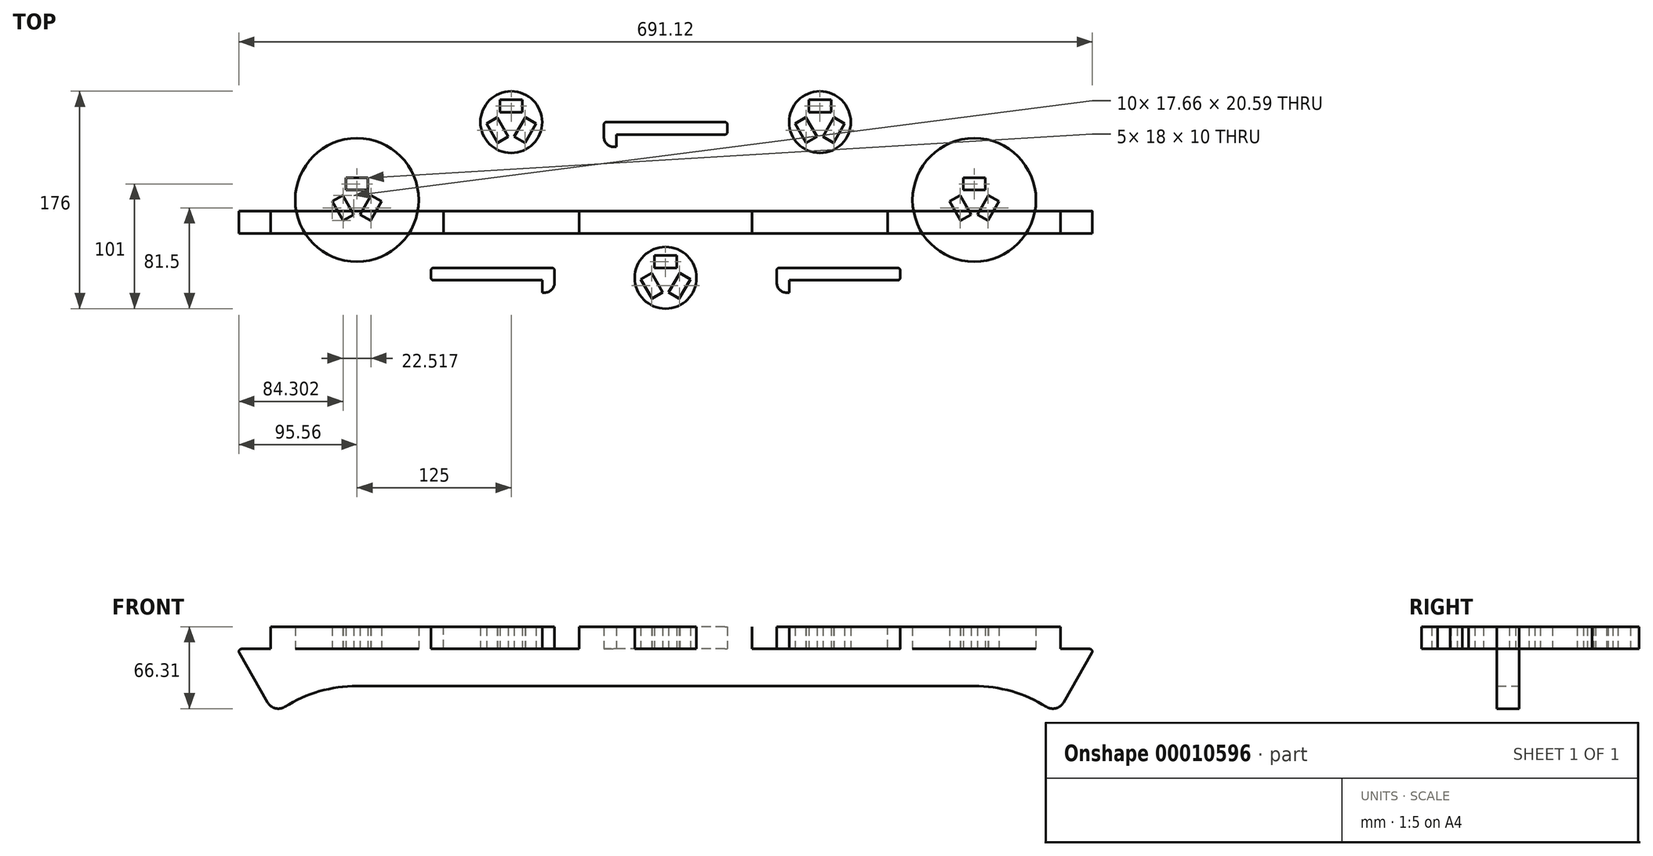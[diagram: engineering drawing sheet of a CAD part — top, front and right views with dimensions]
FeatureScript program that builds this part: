
annotation { "Feature Type Name" : "Feature", "Feature Type Description" : "" }
export const myFeature = defineFeature(function(context is Context, id is Id, definition is map)
    precondition{}
    {
        {
            var Q0;
            Q0=qCreatedBy(makeId("Top.planeOp"),FACE);
            var sketch = newSketch(context, id + "F0", { "sketchPlane" : qUnion([Q0])});
            skLineSegment(sketch, "E0.bottom", {"start": v(-250, 100) * mm, "end": v(250, 100) * mm});
            skLineSegment(sketch, "E0.top", {"start": v(-250, -100) * mm, "end": v(250, -100) * mm});
            skLineSegment(sketch, "E0.left", {"start": v(-250, 100) * mm, "end": v(-250, -100) * mm});
            skLineSegment(sketch, "E0.right", {"start": v(250, 100) * mm, "end": v(250, -100) * mm});
            skLineSegment(sketch, "E1", {"start": v(0, 0) * mm, "end": v(0, 100) * mm, "construction": true});
            skLineSegment(sketch, "E2", {"start": v(250, 0) * mm, "end": v(0, 0) * mm, "construction": true});
            skArc(sketch, "E3", {"start": v(-250, 100) * mm, "mid": v(-350, 0) * mm, "end": v(-250, -100) * mm});
            skArc(sketch, "E4", {"start": v(250, -100) * mm, "mid": v(350, 0) * mm, "end": v(250, 100) * mm});
            skSolve(sketch);
        }
        {
            var Q0;
            Q0=qSketchRegion(id+"F0",true);
            extrude(context, id + "F1", {"entities" : qUnion([Q0]), "depth" : 18 * mm});
        }
        {
            var Q0;
            Q0=qCreatedBy(makeId("Front.planeOp"),FACE);
            cPlane(context, id + "F2", {"entities" : qUnion([Q0]), "cplaneType" : CPlaneType.OFFSET, "offset" : 9 * mm, "width" : 150 * mm, "height" : 150 * mm});
        }
        {
            var Q0;
            Q0=qCreatedBy(makeId("Front.planeOp"),FACE);
            cPlane(context, id + "F3", {"entities" : qUnion([Q0]), "cplaneType" : CPlaneType.OFFSET, "offset" : 9 * mm, "oppositeDirection" : true, "width" : 150 * mm, "height" : 150 * mm});
        }
        {
            var Q0;
            Q0=qCreatedBy(id+"F2.planeOp",FACE);
            var sketch = newSketch(context, id + "F4", { "sketchPlane" : qUnion([Q0])});
            skLineSegment(sketch, "E5.top", {"start": v(-250, -30) * mm, "end": v(0, -30) * mm});
            skLineSegment(sketch, "E6", {"start": v(0, -30) * mm, "end": v(0, 0) * mm, "construction": true});
            skLineSegment(sketch, "E7.top", {"start": v(-320, 18) * mm, "end": v(-180, 18) * mm});
            skLineSegment(sketch, "E7.right", {"start": v(-180, 0) * mm, "end": v(-180, 18) * mm});
            skLineSegment(sketch, "E8.bottom", {"start": v(-70, 0) * mm, "end": v(70, 0) * mm});
            skLineSegment(sketch, "E8.top", {"start": v(-70, 18) * mm, "end": v(70, 18) * mm});
            skLineSegment(sketch, "E8.left", {"start": v(-70, 0) * mm, "end": v(-70, 18) * mm});
            skLineSegment(sketch, "E8.right", {"start": v(70, 0) * mm, "end": v(70, 18) * mm});
            skLineSegment(sketch, "E9", {"start": v(0, 0) * mm, "end": v(0, 18) * mm, "construction": true});
            skLineSegment(sketch, "E10", {"start": v(-317, -52.76) * mm, "end": v(-347, 0) * mm});
            skLineSegment(sketch, "E11.0", {"start": v(-350, 18) * mm, "end": v(-180, 18) * mm, "construction": true});
            skLineSegment(sketch, "E12.trimOffspring", {"start": v(-70, 0) * mm, "end": v(180, 0) * mm});
            skArc(sketch, "E13", {"start": v(-250, -30) * mm, "mid": v(-285.38, -35.85) * mm, "end": v(-317, -52.76) * mm});
            skLineSegment(sketch, "E14", {"start": v(-250, -30) * mm, "end": v(-250, 18) * mm, "construction": true});
            skLineSegment(sketch, "E15.0.MirrorCS", {"start": v(250, -30) * mm, "end": v(0, -30) * mm});
            skArc(sketch, "E16.0.MirrorCS", {"start": v(250, -30) * mm, "mid": v(285.38, -35.85) * mm, "end": v(317, -52.76) * mm});
            skLineSegment(sketch, "E17.0.MirrorCS", {"start": v(317, -52.76) * mm, "end": v(347, 0) * mm});
            skLineSegment(sketch, "E18.0.MirrorCS", {"start": v(320, 18) * mm, "end": v(180, 18) * mm});
            skLineSegment(sketch, "E19.0.MirrorCS", {"start": v(180, 0) * mm, "end": v(180, 18) * mm});
            skLineSegment(sketch, "E20", {"start": v(-180, 0) * mm, "end": v(-70, 0) * mm});
            skLineSegment(sketch, "E21", {"start": v(-320, 18) * mm, "end": v(-320, 0) * mm});
            skLineSegment(sketch, "E22", {"start": v(-320, 0) * mm, "end": v(-347, 0) * mm});
            skLineSegment(sketch, "E23", {"start": v(-320, 0) * mm, "end": v(-180, 0) * mm});
            skLineSegment(sketch, "E24", {"start": v(-350, 18) * mm, "end": v(-350, 0) * mm, "construction": true});
            skLineSegment(sketch, "E25.0.MirrorCS", {"start": v(320, 0) * mm, "end": v(347, 0) * mm});
            skLineSegment(sketch, "E26.0.MirrorCS", {"start": v(320, 18) * mm, "end": v(320, 0) * mm});
            skLineSegment(sketch, "E27.0.MirrorCS", {"start": v(0, 30) * mm, "end": v(0, 0) * mm, "construction": true});
            skLineSegment(sketch, "E28.0.MirrorCS", {"start": v(320, 0) * mm, "end": v(180, 0) * mm});
            skSolve(sketch);
        }
        {
            var Q0;
            Q0=qCreatedBy(id+"F3.planeOp",FACE);
            var sketch = newSketch(context, id + "F5", { "sketchPlane" : qUnion([Q0])});
            skLineSegment(sketch, "E29.0", {"start": v(-320, 18) * mm, "end": v(-180, 18) * mm});
            skLineSegment(sketch, "E29.1", {"start": v(-320, 18) * mm, "end": v(-320, 0) * mm});
            skLineSegment(sketch, "E29.2", {"start": v(-320, 0) * mm, "end": v(-180, 0) * mm});
            skLineSegment(sketch, "E29.3", {"start": v(-180, 0) * mm, "end": v(-180, 18) * mm});
            skLineSegment(sketch, "E29.4", {"start": v(-250, -30) * mm, "end": v(0, -30) * mm});
            skArc(sketch, "E29.5", {"start": v(-250, -30) * mm, "mid": v(-285.38, -35.85) * mm, "end": v(-317, -52.76) * mm});
            skLineSegment(sketch, "E29.6", {"start": v(-317, -52.76) * mm, "end": v(-347, 0) * mm});
            skLineSegment(sketch, "E29.7", {"start": v(-320, 0) * mm, "end": v(-347, 0) * mm});
            skLineSegment(sketch, "E29.8", {"start": v(-180, 0) * mm, "end": v(-70, 0) * mm});
            skLineSegment(sketch, "E29.9", {"start": v(-70, 0) * mm, "end": v(-70, 18) * mm});
            skLineSegment(sketch, "E29.10", {"start": v(-70, 18) * mm, "end": v(70, 18) * mm});
            skLineSegment(sketch, "E29.11", {"start": v(-70, 0) * mm, "end": v(180, 0) * mm});
            skLineSegment(sketch, "E29.12", {"start": v(70, 0) * mm, "end": v(70, 18) * mm});
            skLineSegment(sketch, "E29.13", {"start": v(250, -30) * mm, "end": v(0, -30) * mm});
            skArc(sketch, "E29.14", {"start": v(250, -30) * mm, "mid": v(285.38, -35.85) * mm, "end": v(317, -52.76) * mm});
            skLineSegment(sketch, "E29.15", {"start": v(317, -52.76) * mm, "end": v(347, 0) * mm});
            skLineSegment(sketch, "E29.16", {"start": v(320, 0) * mm, "end": v(347, 0) * mm});
            skLineSegment(sketch, "E29.17", {"start": v(320, 0) * mm, "end": v(180, 0) * mm});
            skLineSegment(sketch, "E29.18", {"start": v(320, 18) * mm, "end": v(180, 18) * mm});
            skLineSegment(sketch, "E29.19", {"start": v(320, 18) * mm, "end": v(320, 0) * mm});
            skLineSegment(sketch, "E29.20", {"start": v(180, 0) * mm, "end": v(180, 18) * mm});
            skSolve(sketch);
        }
        {
            var Q0;
            Q0=qSketchRegion(id+"F4",true);
            extrude(context, id + "F6", {"entities" : qUnion([Q0]), "depth" : 18 * mm});
        }
        {
            var Q0;
            Q0 = qSketchRegion(id + "F5", true);
            extrude(context, id + "F7", {"entities" : qUnion([Q0]), "operationType" : NewBodyOperationType.ADD, "oppositeDirection" : true, "depth" : 18 * mm});
        }
        {
            var Q0;
            Q0=makeQuery(id+"F6.opExtrude","SWEPT_EDGE",EDGE,{"disambiguationData":[OSD([sQuery(id+"F4.wireOp",EDGE,"E10"),sQuery(id+"F4.wireOp",EDGE,"E13")])]});
            var Q1;
            Q1=makeQuery(id+"F6.opExtrude","SWEPT_EDGE",EDGE,{"disambiguationData":[OSD([sQuery(id+"F4.wireOp",EDGE,"E16.0.MirrorCS"),sQuery(id+"F4.wireOp",EDGE,"E17.0.MirrorCS")])]});
            var Q2;
            Q2=makeQuery(id+"F7.opExtrude","SWEPT_EDGE",EDGE,{"disambiguationData":[OSD([sQuery(id+"F5.wireOp",EDGE,"E29.5"),sQuery(id+"F5.wireOp",EDGE,"E29.6")])]});
            var Q3;
            Q3=makeQuery(id+"F7.opExtrude","SWEPT_EDGE",EDGE,{"disambiguationData":[OSD([sQuery(id+"F5.wireOp",EDGE,"E29.14"),sQuery(id+"F5.wireOp",EDGE,"E29.15")])]});
            fillet(context, id + "F8", {"entities" : qUnion([Q0, Q1, Q2, Q3]), "radius" : 10 * mm, "tangentPropagation" : true, "allowEdgeOverflow" : false});
        }
        {
            var Q0;
            Q0=makeQuery(id+"F6.opExtrude","SWEPT_EDGE",EDGE,{"disambiguationData":[OSD([sQuery(id+"F4.wireOp",EDGE,"E10"),sQuery(id+"F4.wireOp",EDGE,"E22")])]});
            var Q1;
            Q1=makeQuery(id+"F6.opExtrude","SWEPT_EDGE",EDGE,{"disambiguationData":[OSD([sQuery(id+"F4.wireOp",EDGE,"E17.0.MirrorCS"),sQuery(id+"F4.wireOp",EDGE,"E25.0.MirrorCS")])]});
            var Q2;
            Q2=makeQuery(id+"F7.opExtrude","SWEPT_EDGE",EDGE,{"disambiguationData":[OSD([sQuery(id+"F5.wireOp",EDGE,"E29.6"),sQuery(id+"F5.wireOp",EDGE,"E29.7")])]});
            var Q3;
            Q3=makeQuery(id+"F7.opExtrude","SWEPT_EDGE",EDGE,{"disambiguationData":[OSD([sQuery(id+"F5.wireOp",EDGE,"E29.15"),sQuery(id+"F5.wireOp",EDGE,"E29.16")])]});
            fillet(context, id + "F9", {"entities" : qUnion([Q0, Q1, Q2, Q3]), "radius" : 2 * mm, "tangentPropagation" : true, "allowEdgeOverflow" : false});
        }
        {
            var Q0;
            Q0=makeQuery(id+"F7.opExtrude","SWEPT_BODY",BODY,{"disambiguationData":[OSD([sQuery(id+"F5.wireOp",EDGE,"E29.0"),sQuery(id+"F5.wireOp",EDGE,"E29.1"),sQuery(id+"F5.wireOp",EDGE,"E29.3"),sQuery(id+"F5.wireOp",EDGE,"E29.4"),sQuery(id+"F5.wireOp",EDGE,"E29.5"),sQuery(id+"F5.wireOp",EDGE,"E29.6"),sQuery(id+"F5.wireOp",EDGE,"E29.7"),sQuery(id+"F5.wireOp",EDGE,"E29.8"),sQuery(id+"F5.wireOp",EDGE,"E29.9"),sQuery(id+"F5.wireOp",EDGE,"E29.10"),sQuery(id+"F5.wireOp",EDGE,"E29.11"),sQuery(id+"F5.wireOp",EDGE,"E29.12"),sQuery(id+"F5.wireOp",EDGE,"E29.13"),sQuery(id+"F5.wireOp",EDGE,"E29.14"),sQuery(id+"F5.wireOp",EDGE,"E29.15"),sQuery(id+"F5.wireOp",EDGE,"E29.16"),sQuery(id+"F5.wireOp",EDGE,"E29.18"),sQuery(id+"F5.wireOp",EDGE,"E29.19"),sQuery(id+"F5.wireOp",EDGE,"E29.20")])]});
            var Q1;
            Q1=makeQuery(id+"F6.opExtrude","SWEPT_BODY",BODY,{"disambiguationData":[OSD([sQuery(id+"F4.wireOp",EDGE,"E5.top"),sQuery(id+"F4.wireOp",EDGE,"E7.top"),sQuery(id+"F4.wireOp",EDGE,"E7.right"),sQuery(id+"F4.wireOp",EDGE,"E8.top"),sQuery(id+"F4.wireOp",EDGE,"E8.left"),sQuery(id+"F4.wireOp",EDGE,"E8.right"),sQuery(id+"F4.wireOp",EDGE,"E10"),sQuery(id+"F4.wireOp",EDGE,"E12.trimOffspring"),sQuery(id+"F4.wireOp",EDGE,"E13"),sQuery(id+"F4.wireOp",EDGE,"E15.0.MirrorCS"),sQuery(id+"F4.wireOp",EDGE,"E16.0.MirrorCS"),sQuery(id+"F4.wireOp",EDGE,"E17.0.MirrorCS"),sQuery(id+"F4.wireOp",EDGE,"E18.0.MirrorCS"),sQuery(id+"F4.wireOp",EDGE,"E19.0.MirrorCS"),sQuery(id+"F4.wireOp",EDGE,"E20"),sQuery(id+"F4.wireOp",EDGE,"E21"),sQuery(id+"F4.wireOp",EDGE,"E22"),sQuery(id+"F4.wireOp",EDGE,"E25.0.MirrorCS"),sQuery(id+"F4.wireOp",EDGE,"E26.0.MirrorCS")])]});
            var Q2;
            Q2=makeQuery(id+"F1.opExtrude","SWEPT_BODY",BODY,{"disambiguationData":[OSD([sQuery(id+"F0.wireOp",EDGE,"E0.bottom"),sQuery(id+"F0.wireOp",EDGE,"E0.top"),sQuery(id+"F0.wireOp",EDGE,"E3"),sQuery(id+"F0.wireOp",EDGE,"E4")])]});
            booleanBodies(context, id + "F10", {"operationType" : BooleanOperationType.SUBTRACTION, "tools" : qUnion([Q0, Q1]), "targets" : qUnion([Q2]), "keepTools" : true});
        }
        {
            var Q0;
            Q0=qCreatedBy(makeId("Top.planeOp"),FACE);
            var sketch = newSketch(context, id + "F11", { "sketchPlane" : qUnion([Q0])});
            skLineSegment(sketch, "E30", {"start": v(125, 63) * mm, "end": v(0, 63) * mm, "construction": true});
            skLineSegment(sketch, "E31", {"start": v(0, 63) * mm, "end": v(-125, 63) * mm, "construction": true});
            skLineSegment(sketch, "E32", {"start": v(0, 0) * mm, "end": v(0, 63) * mm, "construction": true});
            skLineSegment(sketch, "E33", {"start": v(0, -63) * mm, "end": v(0, 0) * mm, "construction": true});
            skLineSegment(sketch, "E34", {"start": v(0, -63) * mm, "end": v(-125, 63) * mm, "construction": true});
            skLineSegment(sketch, "E35", {"start": v(0, -63) * mm, "end": v(125, 63) * mm, "construction": true});
            skLineSegment(sketch, "E36", {"start": v(-250, -9) * mm, "end": v(-250, 0) * mm, "construction": true});
            skLineSegment(sketch, "E37", {"start": v(-250, 0) * mm, "end": v(0, 0) * mm, "construction": true});
            skCircle(sketch, "E38", {"center": v(-125, 63) * mm, "radius": 25 * mm});
            skLineSegment(sketch, "E39.bottom", {"start": v(-134, 81) * mm, "end": v(-116, 81) * mm});
            skLineSegment(sketch, "E39.top", {"start": v(-134, 71) * mm, "end": v(-116, 71) * mm});
            skLineSegment(sketch, "E39.left", {"start": v(-134, 81) * mm, "end": v(-134, 71) * mm});
            skLineSegment(sketch, "E39.right", {"start": v(-116, 81) * mm, "end": v(-116, 71) * mm});
            skLineSegment(sketch, "E40", {"start": v(-125, 63) * mm, "end": v(-125, 71) * mm});
            skLineSegment(sketch, "E41.1.0", {"start": v(-136.09, 46.2) * mm, "end": v(-145.09, 61.8) * mm});
            skLineSegment(sketch, "E41.1.1", {"start": v(-145.09, 61.8) * mm, "end": v(-136.43, 66.8) * mm});
            skLineSegment(sketch, "E41.1.2", {"start": v(-127.43, 51.2) * mm, "end": v(-136.43, 66.8) * mm});
            skLineSegment(sketch, "E41.1.3", {"start": v(-136.09, 46.2) * mm, "end": v(-127.43, 51.2) * mm});
            skLineSegment(sketch, "E41.2.0", {"start": v(-104.91, 61.8) * mm, "end": v(-113.91, 46.2) * mm});
            skLineSegment(sketch, "E41.2.1", {"start": v(-113.91, 46.2) * mm, "end": v(-122.57, 51.2) * mm});
            skLineSegment(sketch, "E41.2.2", {"start": v(-113.57, 66.8) * mm, "end": v(-122.57, 51.2) * mm});
            skLineSegment(sketch, "E41.2.3", {"start": v(-104.91, 61.8) * mm, "end": v(-113.57, 66.8) * mm});
            skLineSegment(sketch, "E42.2.2", {"start": v(136.43, 66.8) * mm, "end": v(127.43, 51.2) * mm});
            skLineSegment(sketch, "E43.right", {"start": v(134, 81) * mm, "end": v(134, 71) * mm});
            skLineSegment(sketch, "E43.bottom", {"start": v(116, 81) * mm, "end": v(134, 81) * mm});
            skPoint(sketch, "E42.center", {"position": v(125, 63) * mm});
            skLineSegment(sketch, "E42.2.0", {"start": v(145.09, 61.8) * mm, "end": v(136.09, 46.2) * mm});
            skLineSegment(sketch, "E42.2.1", {"start": v(136.09, 46.2) * mm, "end": v(127.43, 51.2) * mm});
            skLineSegment(sketch, "E44", {"start": v(125, 63) * mm, "end": v(125, 71) * mm});
            skLineSegment(sketch, "E42.1.0", {"start": v(113.91, 46.2) * mm, "end": v(104.91, 61.8) * mm});
            skLineSegment(sketch, "E42.1.1", {"start": v(104.91, 61.8) * mm, "end": v(113.57, 66.8) * mm});
            skLineSegment(sketch, "E42.1.2", {"start": v(122.57, 51.2) * mm, "end": v(113.57, 66.8) * mm});
            skLineSegment(sketch, "E42.2.3", {"start": v(145.09, 61.8) * mm, "end": v(136.43, 66.8) * mm});
            skCircle(sketch, "E45", {"center": v(125, 63) * mm, "radius": 25 * mm});
            skLineSegment(sketch, "E43.left", {"start": v(116, 81) * mm, "end": v(116, 71) * mm});
            skLineSegment(sketch, "E42.1.3", {"start": v(113.91, 46.2) * mm, "end": v(122.57, 51.2) * mm});
            skLineSegment(sketch, "E43.top", {"start": v(116, 71) * mm, "end": v(134, 71) * mm});
            skLineSegment(sketch, "E46.2.2", {"start": v(11.43, -59.2) * mm, "end": v(2.43, -74.8) * mm});
            skLineSegment(sketch, "E47.right", {"start": v(9, -45) * mm, "end": v(9, -55) * mm});
            skLineSegment(sketch, "E47.bottom", {"start": v(-9, -45) * mm, "end": v(9, -45) * mm});
            skPoint(sketch, "E46.center", {"position": v(0, -63) * mm});
            skLineSegment(sketch, "E46.2.0", {"start": v(20.09, -64.2) * mm, "end": v(11.09, -79.8) * mm});
            skLineSegment(sketch, "E46.2.1", {"start": v(11.09, -79.8) * mm, "end": v(2.43, -74.8) * mm});
            skLineSegment(sketch, "E48", {"start": v(0, -63) * mm, "end": v(0, -55) * mm});
            skLineSegment(sketch, "E46.1.0", {"start": v(-11.09, -79.8) * mm, "end": v(-20.09, -64.2) * mm});
            skLineSegment(sketch, "E46.1.1", {"start": v(-20.09, -64.2) * mm, "end": v(-11.43, -59.2) * mm});
            skLineSegment(sketch, "E46.1.2", {"start": v(-2.43, -74.8) * mm, "end": v(-11.43, -59.2) * mm});
            skLineSegment(sketch, "E46.2.3", {"start": v(20.09, -64.2) * mm, "end": v(11.43, -59.2) * mm});
            skCircle(sketch, "E49", {"center": v(0, -63) * mm, "radius": 25 * mm});
            skLineSegment(sketch, "E47.left", {"start": v(-9, -45) * mm, "end": v(-9, -55) * mm});
            skLineSegment(sketch, "E46.1.3", {"start": v(-11.09, -79.8) * mm, "end": v(-2.43, -74.8) * mm});
            skLineSegment(sketch, "E47.top", {"start": v(-9, -55) * mm, "end": v(9, -55) * mm});
            skLineSegment(sketch, "E50.2.2", {"start": v(-238.57, 3.8) * mm, "end": v(-247.57, -11.8) * mm});
            skLineSegment(sketch, "E51.right", {"start": v(-241, 18) * mm, "end": v(-241, 8) * mm});
            skLineSegment(sketch, "E51.bottom", {"start": v(-259, 18) * mm, "end": v(-241, 18) * mm});
            skPoint(sketch, "E50.center", {"position": v(-250, 0) * mm});
            skLineSegment(sketch, "E50.2.0", {"start": v(-229.91, -1.2) * mm, "end": v(-238.91, -16.8) * mm});
            skLineSegment(sketch, "E50.2.1", {"start": v(-238.91, -16.8) * mm, "end": v(-247.57, -11.8) * mm});
            skLineSegment(sketch, "E52", {"start": v(-250, 0) * mm, "end": v(-250, 8) * mm});
            skLineSegment(sketch, "E50.1.0", {"start": v(-261.09, -16.8) * mm, "end": v(-270.09, -1.2) * mm});
            skLineSegment(sketch, "E50.1.1", {"start": v(-270.09, -1.2) * mm, "end": v(-261.43, 3.8) * mm});
            skLineSegment(sketch, "E50.1.2", {"start": v(-252.43, -11.8) * mm, "end": v(-261.43, 3.8) * mm});
            skLineSegment(sketch, "E50.2.3", {"start": v(-229.91, -1.2) * mm, "end": v(-238.57, 3.8) * mm});
            skCircle(sketch, "E53", {"center": v(-250, 0) * mm, "radius": 50 * mm});
            skLineSegment(sketch, "E51.left", {"start": v(-259, 18) * mm, "end": v(-259, 8) * mm});
            skLineSegment(sketch, "E50.1.3", {"start": v(-261.09, -16.8) * mm, "end": v(-252.43, -11.8) * mm});
            skLineSegment(sketch, "E51.top", {"start": v(-259, 8) * mm, "end": v(-241, 8) * mm});
            skLineSegment(sketch, "E54.0.MirrorCS", {"start": v(250, -9) * mm, "end": v(250, 0) * mm, "construction": true});
            skLineSegment(sketch, "E54.1.MirrorCS", {"start": v(270.09, -1.2) * mm, "end": v(261.43, 3.8) * mm});
            skLineSegment(sketch, "E54.2.MirrorCS", {"start": v(238.57, 3.8) * mm, "end": v(247.57, -11.8) * mm});
            skLineSegment(sketch, "E54.3.MirrorCS", {"start": v(250, 0) * mm, "end": v(250, 8) * mm});
            skLineSegment(sketch, "E54.4.MirrorCS", {"start": v(259, 18) * mm, "end": v(259, 8) * mm});
            skLineSegment(sketch, "E54.5.MirrorCS", {"start": v(259, 8) * mm, "end": v(241, 8) * mm});
            skLineSegment(sketch, "E54.6.MirrorCS", {"start": v(259, 18) * mm, "end": v(241, 18) * mm});
            skLineSegment(sketch, "E54.7.MirrorCS", {"start": v(241, 18) * mm, "end": v(241, 8) * mm});
            skPoint(sketch, "E54.8.MirrorP", {"position": v(250, 0) * mm});
            skLineSegment(sketch, "E54.9.MirrorCS", {"start": v(261.09, -16.8) * mm, "end": v(270.09, -1.2) * mm});
            skLineSegment(sketch, "E54.10.MirrorCS", {"start": v(252.43, -11.8) * mm, "end": v(261.43, 3.8) * mm});
            skLineSegment(sketch, "E54.11.MirrorCS", {"start": v(238.91, -16.8) * mm, "end": v(247.57, -11.8) * mm});
            skLineSegment(sketch, "E54.12.MirrorCS", {"start": v(261.09, -16.8) * mm, "end": v(252.43, -11.8) * mm});
            skLineSegment(sketch, "E54.13.MirrorCS", {"start": v(229.91, -1.2) * mm, "end": v(238.57, 3.8) * mm});
            skLineSegment(sketch, "E54.14.MirrorCS", {"start": v(229.91, -1.2) * mm, "end": v(238.91, -16.8) * mm});
            skCircle(sketch, "E54.15.MirrorC", {"center": v(250, 0) * mm, "radius": 50 * mm});
            skLineSegment(sketch, "E55.bottom", {"start": v(188, -65) * mm, "end": v(100, -65) * mm});
            skLineSegment(sketch, "E55.top", {"start": v(188, -55) * mm, "end": v(100, -55) * mm});
            skLineSegment(sketch, "E55.left", {"start": v(190, -63) * mm, "end": v(190, -57) * mm});
            skLineSegment(sketch, "E56.bottom", {"start": v(100, -55) * mm, "end": v(92, -55) * mm});
            skLineSegment(sketch, "E56.top", {"start": v(100, -75) * mm, "end": v(98, -75) * mm});
            skLineSegment(sketch, "E56.left", {"start": v(100, -65) * mm, "end": v(100, -75) * mm});
            skLineSegment(sketch, "E56.right", {"start": v(90, -57) * mm, "end": v(90, -67) * mm});
            skPoint(sketch, "E57.visualSharp", {"position": v(90, -75) * mm});
            skArc(sketch, "E57.filletArc", {"start": v(90, -67) * mm, "mid": v(92.34, -72.66) * mm, "end": v(98, -75) * mm});
            skPoint(sketch, "E58.visualSharp", {"position": v(190, -65) * mm});
            skArc(sketch, "E58.filletArc", {"start": v(188, -65) * mm, "mid": v(189.41, -64.41) * mm, "end": v(190, -63) * mm});
            skPoint(sketch, "E59.visualSharp", {"position": v(190, -55) * mm});
            skArc(sketch, "E59.filletArc", {"start": v(190, -57) * mm, "mid": v(189.41, -55.59) * mm, "end": v(188, -55) * mm});
            skPoint(sketch, "E60.visualSharp", {"position": v(90, -55) * mm});
            skArc(sketch, "E60.filletArc", {"start": v(92, -55) * mm, "mid": v(90.59, -55.59) * mm, "end": v(90, -57) * mm});
            skLineSegment(sketch, "E61.0.MirrorCS", {"start": v(-90, -57) * mm, "end": v(-90, -67) * mm});
            skLineSegment(sketch, "E61.1.MirrorCS", {"start": v(-100, -55) * mm, "end": v(-92, -55) * mm});
            skLineSegment(sketch, "E61.2.MirrorCS", {"start": v(-190, -63) * mm, "end": v(-190, -57) * mm});
            skArc(sketch, "E61.3.MirrorCS", {"start": v(-190, -57) * mm, "mid": v(-189.41, -55.59) * mm, "end": v(-188, -55) * mm});
            skLineSegment(sketch, "E61.4.MirrorCS", {"start": v(-100, -65) * mm, "end": v(-100, -75) * mm});
            skLineSegment(sketch, "E61.5.MirrorCS", {"start": v(-188, -55) * mm, "end": v(-100, -55) * mm});
            skArc(sketch, "E61.6.MirrorCS", {"start": v(-92, -55) * mm, "mid": v(-90.59, -55.59) * mm, "end": v(-90, -57) * mm});
            skPoint(sketch, "E61.7.MirrorP", {"position": v(-90, -55) * mm});
            skPoint(sketch, "E61.8.MirrorP", {"position": v(-190, -55) * mm});
            skLineSegment(sketch, "E61.9.MirrorCS", {"start": v(-188, -65) * mm, "end": v(-100, -65) * mm});
            skArc(sketch, "E61.10.MirrorCS", {"start": v(-188, -65) * mm, "mid": v(-189.41, -64.41) * mm, "end": v(-190, -63) * mm});
            skPoint(sketch, "E61.11.MirrorP", {"position": v(-90, -75) * mm});
            skPoint(sketch, "E61.12.MirrorP", {"position": v(-190, -65) * mm});
            skArc(sketch, "E61.13.MirrorCS", {"start": v(-90, -67) * mm, "mid": v(-92.34, -72.66) * mm, "end": v(-98, -75) * mm});
            skLineSegment(sketch, "E61.14.MirrorCS", {"start": v(-100, -75) * mm, "end": v(-98, -75) * mm});
            skPoint(sketch, "E62.visualSharp", {"position": v(50, 53) * mm});
            skPoint(sketch, "E63.visualSharp", {"position": v(-50, 43) * mm});
            skLineSegment(sketch, "E64.right", {"start": v(-50, 61) * mm, "end": v(-50, 51) * mm});
            skArc(sketch, "E62.filletArc", {"start": v(48, 53) * mm, "mid": v(49.41, 53.59) * mm, "end": v(50, 55) * mm});
            skLineSegment(sketch, "E65.left", {"start": v(50, 55) * mm, "end": v(50, 61) * mm});
            skPoint(sketch, "E66.visualSharp", {"position": v(50, 63.57) * mm});
            skPoint(sketch, "E67.visualSharp", {"position": v(-50, 59.42) * mm});
            skLineSegment(sketch, "E65.bottom", {"start": v(48, 53) * mm, "end": v(-40, 53) * mm});
            skArc(sketch, "E66.filletArc", {"start": v(50, 61) * mm, "mid": v(49.41, 62.41) * mm, "end": v(48, 63) * mm});
            skLineSegment(sketch, "E64.left", {"start": v(-40, 53) * mm, "end": v(-40, 43) * mm});
            skArc(sketch, "E63.filletArc", {"start": v(-50, 51) * mm, "mid": v(-47.66, 45.34) * mm, "end": v(-42, 43) * mm});
            skArc(sketch, "E67.filletArc", {"start": v(-48, 63) * mm, "mid": v(-49.41, 62.41) * mm, "end": v(-50, 61) * mm});
            skLineSegment(sketch, "E64.top", {"start": v(-40, 43) * mm, "end": v(-42, 43) * mm});
            skLineSegment(sketch, "E68", {"start": v(48, 63) * mm, "end": v(-48, 63) * mm});
            skSolve(sketch);
        }
        {
            var Q0;
            Q0 = qSketchRegion(id + "F11", true);
            var Q1;
            Q1=makeQuery(id+"F1.opExtrude","CAP_FACE",FACE,{"disambiguationData":[OSD([sQuery(id+"F0.wireOp",EDGE,"E0.bottom"),sQuery(id+"F0.wireOp",EDGE,"E0.top"),sQuery(id+"F0.wireOp",EDGE,"E3"),sQuery(id+"F0.wireOp",EDGE,"E4")])],"isStart":false});
            extrude(context, id + "F12", {"entities" : qUnion([Q0]), "endBound" : BoundingType.UP_TO_SURFACE, "endBoundEntityFace" : qUnion([Q1]), "depth" : 25 * mm});
        }
        {
            var Q0;
            Q0=makeQuery(id+"F12.opExtrude","SWEPT_BODY",BODY,{"disambiguationData":[OSD([sQuery(id+"F11.wireOp",EDGE,"E54.1.MirrorCS"),sQuery(id+"F11.wireOp",EDGE,"E54.2.MirrorCS"),sQuery(id+"F11.wireOp",EDGE,"E54.4.MirrorCS"),sQuery(id+"F11.wireOp",EDGE,"E54.5.MirrorCS"),sQuery(id+"F11.wireOp",EDGE,"E54.6.MirrorCS"),sQuery(id+"F11.wireOp",EDGE,"E54.7.MirrorCS"),sQuery(id+"F11.wireOp",EDGE,"E54.9.MirrorCS"),sQuery(id+"F11.wireOp",EDGE,"E54.10.MirrorCS"),sQuery(id+"F11.wireOp",EDGE,"E54.11.MirrorCS"),sQuery(id+"F11.wireOp",EDGE,"E54.12.MirrorCS"),sQuery(id+"F11.wireOp",EDGE,"E54.13.MirrorCS"),sQuery(id+"F11.wireOp",EDGE,"E54.14.MirrorCS"),sQuery(id+"F11.wireOp",EDGE,"E54.15.MirrorC")])]});
            var Q1;
            Q1=makeQuery(id+"F12.opExtrude","SWEPT_BODY",BODY,{"disambiguationData":[OSD([sQuery(id+"F11.wireOp",EDGE,"E42.2.2"),sQuery(id+"F11.wireOp",EDGE,"E43.right"),sQuery(id+"F11.wireOp",EDGE,"E43.bottom"),sQuery(id+"F11.wireOp",EDGE,"E42.2.0"),sQuery(id+"F11.wireOp",EDGE,"E42.2.1"),sQuery(id+"F11.wireOp",EDGE,"E42.1.0"),sQuery(id+"F11.wireOp",EDGE,"E42.1.1"),sQuery(id+"F11.wireOp",EDGE,"E42.1.2"),sQuery(id+"F11.wireOp",EDGE,"E42.2.3"),sQuery(id+"F11.wireOp",EDGE,"E45"),sQuery(id+"F11.wireOp",EDGE,"E43.left"),sQuery(id+"F11.wireOp",EDGE,"E42.1.3"),sQuery(id+"F11.wireOp",EDGE,"E43.top")])]});
            var Q2;
            Q2=makeQuery(id+"F12.opExtrude","SWEPT_BODY",BODY,{"disambiguationData":[OSD([sQuery(id+"F11.wireOp",EDGE,"E46.2.2"),sQuery(id+"F11.wireOp",EDGE,"E47.right"),sQuery(id+"F11.wireOp",EDGE,"E47.bottom"),sQuery(id+"F11.wireOp",EDGE,"E46.2.0"),sQuery(id+"F11.wireOp",EDGE,"E46.2.1"),sQuery(id+"F11.wireOp",EDGE,"E46.1.0"),sQuery(id+"F11.wireOp",EDGE,"E46.1.1"),sQuery(id+"F11.wireOp",EDGE,"E46.1.2"),sQuery(id+"F11.wireOp",EDGE,"E46.2.3"),sQuery(id+"F11.wireOp",EDGE,"E49"),sQuery(id+"F11.wireOp",EDGE,"E47.left"),sQuery(id+"F11.wireOp",EDGE,"E46.1.3"),sQuery(id+"F11.wireOp",EDGE,"E47.top")])]});
            var Q3;
            Q3=makeQuery(id+"F12.opExtrude","SWEPT_BODY",BODY,{"disambiguationData":[OSD([sQuery(id+"F11.wireOp",EDGE,"E38"),sQuery(id+"F11.wireOp",EDGE,"E39.bottom"),sQuery(id+"F11.wireOp",EDGE,"E39.top"),sQuery(id+"F11.wireOp",EDGE,"E39.left"),sQuery(id+"F11.wireOp",EDGE,"E39.right"),sQuery(id+"F11.wireOp",EDGE,"E41.1.0"),sQuery(id+"F11.wireOp",EDGE,"E41.1.1"),sQuery(id+"F11.wireOp",EDGE,"E41.1.2"),sQuery(id+"F11.wireOp",EDGE,"E41.1.3"),sQuery(id+"F11.wireOp",EDGE,"E41.2.0"),sQuery(id+"F11.wireOp",EDGE,"E41.2.1"),sQuery(id+"F11.wireOp",EDGE,"E41.2.2"),sQuery(id+"F11.wireOp",EDGE,"E41.2.3")])]});
            var Q4;
            Q4=makeQuery(id+"F12.opExtrude","SWEPT_BODY",BODY,{"disambiguationData":[OSD([sQuery(id+"F11.wireOp",EDGE,"E50.2.2"),sQuery(id+"F11.wireOp",EDGE,"E51.right"),sQuery(id+"F11.wireOp",EDGE,"E51.bottom"),sQuery(id+"F11.wireOp",EDGE,"E50.2.0"),sQuery(id+"F11.wireOp",EDGE,"E50.2.1"),sQuery(id+"F11.wireOp",EDGE,"E50.1.0"),sQuery(id+"F11.wireOp",EDGE,"E50.1.1"),sQuery(id+"F11.wireOp",EDGE,"E50.1.2"),sQuery(id+"F11.wireOp",EDGE,"E50.2.3"),sQuery(id+"F11.wireOp",EDGE,"E53"),sQuery(id+"F11.wireOp",EDGE,"E51.left"),sQuery(id+"F11.wireOp",EDGE,"E50.1.3"),sQuery(id+"F11.wireOp",EDGE,"E51.top")])]});
            var Q5;
            Q5=makeQuery(id+"F12.opExtrude","SWEPT_BODY",BODY,{"disambiguationData":[OSD([sQuery(id+"F11.wireOp",EDGE,"E55.bottom"),sQuery(id+"F11.wireOp",EDGE,"E55.top"),sQuery(id+"F11.wireOp",EDGE,"E55.left"),sQuery(id+"F11.wireOp",EDGE,"E56.bottom"),sQuery(id+"F11.wireOp",EDGE,"E56.top"),sQuery(id+"F11.wireOp",EDGE,"E56.left"),sQuery(id+"F11.wireOp",EDGE,"E56.right"),sQuery(id+"F11.wireOp",EDGE,"E57.filletArc"),sQuery(id+"F11.wireOp",EDGE,"E58.filletArc"),sQuery(id+"F11.wireOp",EDGE,"E59.filletArc"),sQuery(id+"F11.wireOp",EDGE,"E60.filletArc")])]});
            var Q6;
            Q6=makeQuery(id+"F12.opExtrude","SWEPT_BODY",BODY,{"disambiguationData":[OSD([sQuery(id+"F11.wireOp",EDGE,"E61.0.MirrorCS"),sQuery(id+"F11.wireOp",EDGE,"E61.1.MirrorCS"),sQuery(id+"F11.wireOp",EDGE,"E61.2.MirrorCS"),sQuery(id+"F11.wireOp",EDGE,"E61.3.MirrorCS"),sQuery(id+"F11.wireOp",EDGE,"E61.4.MirrorCS"),sQuery(id+"F11.wireOp",EDGE,"E61.5.MirrorCS"),sQuery(id+"F11.wireOp",EDGE,"E61.6.MirrorCS"),sQuery(id+"F11.wireOp",EDGE,"E61.9.MirrorCS"),sQuery(id+"F11.wireOp",EDGE,"E61.10.MirrorCS"),sQuery(id+"F11.wireOp",EDGE,"E61.13.MirrorCS"),sQuery(id+"F11.wireOp",EDGE,"E61.14.MirrorCS")])]});
            var Q7;
            Q7=makeQuery(id+"F12.opExtrude","SWEPT_BODY",BODY,{"disambiguationData":[OSD([sQuery(id+"F11.wireOp",EDGE,"E64.right"),sQuery(id+"F11.wireOp",EDGE,"E62.filletArc"),sQuery(id+"F11.wireOp",EDGE,"E65.left"),sQuery(id+"F11.wireOp",EDGE,"E65.bottom"),sQuery(id+"F11.wireOp",EDGE,"E66.filletArc"),sQuery(id+"F11.wireOp",EDGE,"E64.left"),sQuery(id+"F11.wireOp",EDGE,"E63.filletArc"),sQuery(id+"F11.wireOp",EDGE,"E67.filletArc"),sQuery(id+"F11.wireOp",EDGE,"E64.top"),sQuery(id+"F11.wireOp",EDGE,"E68")])]});
            var Q8;
            Q8=makeQuery(id+"F1.opExtrude","SWEPT_BODY",BODY,{"disambiguationData":[OSD([sQuery(id+"F0.wireOp",EDGE,"E0.bottom"),sQuery(id+"F0.wireOp",EDGE,"E0.top"),sQuery(id+"F0.wireOp",EDGE,"E3"),sQuery(id+"F0.wireOp",EDGE,"E4")])]});
            booleanBodies(context, id + "F13", {"operationType" : BooleanOperationType.SUBTRACTION, "tools" : qUnion([Q0, Q1, Q2, Q3, Q4, Q5, Q6, Q7]), "targets" : qUnion([Q8]), "keepTools" : true});
        }
        {
            var Q0;
            Q0=makeQuery(id+"F13.opBoolean","SPLIT",BODY,{"disambiguationData":[OD(12.0)],"derivedFrom":makeQuery(id+"F1.opExtrude","SWEPT_BODY",BODY,{"disambiguationData":[OSD([sQuery(id+"F0.wireOp",EDGE,"E0.bottom"),sQuery(id+"F0.wireOp",EDGE,"E0.top"),sQuery(id+"F0.wireOp",EDGE,"E3"),sQuery(id+"F0.wireOp",EDGE,"E4")])]})});
            var Q1;
            Q1=makeQuery(id+"F13.opBoolean","SPLIT",BODY,{"disambiguationData":[OD(13.0)],"derivedFrom":makeQuery(id+"F1.opExtrude","SWEPT_BODY",BODY,{"disambiguationData":[OSD([sQuery(id+"F0.wireOp",EDGE,"E0.bottom"),sQuery(id+"F0.wireOp",EDGE,"E0.top"),sQuery(id+"F0.wireOp",EDGE,"E3"),sQuery(id+"F0.wireOp",EDGE,"E4")])]})});
            var Q2;
            Q2=makeQuery(id+"F13.opBoolean","SPLIT",BODY,{"disambiguationData":[OD(14.0)],"derivedFrom":makeQuery(id+"F1.opExtrude","SWEPT_BODY",BODY,{"disambiguationData":[OSD([sQuery(id+"F0.wireOp",EDGE,"E0.bottom"),sQuery(id+"F0.wireOp",EDGE,"E0.top"),sQuery(id+"F0.wireOp",EDGE,"E3"),sQuery(id+"F0.wireOp",EDGE,"E4")])]})});
            var Q3;
            Q3=makeQuery(id+"F13.opBoolean","SPLIT",BODY,{"disambiguationData":[OD(5.0)],"derivedFrom":makeQuery(id+"F1.opExtrude","SWEPT_BODY",BODY,{"disambiguationData":[OSD([sQuery(id+"F0.wireOp",EDGE,"E0.bottom"),sQuery(id+"F0.wireOp",EDGE,"E0.top"),sQuery(id+"F0.wireOp",EDGE,"E3"),sQuery(id+"F0.wireOp",EDGE,"E4")])]})});
            var Q4;
            Q4=makeQuery(id+"F13.opBoolean","SPLIT",BODY,{"disambiguationData":[OD(3.0)],"derivedFrom":makeQuery(id+"F1.opExtrude","SWEPT_BODY",BODY,{"disambiguationData":[OSD([sQuery(id+"F0.wireOp",EDGE,"E0.bottom"),sQuery(id+"F0.wireOp",EDGE,"E0.top"),sQuery(id+"F0.wireOp",EDGE,"E3"),sQuery(id+"F0.wireOp",EDGE,"E4")])]})});
            var Q5;
            Q5=makeQuery(id+"F13.opBoolean","SPLIT",BODY,{"disambiguationData":[OD(4.0)],"derivedFrom":makeQuery(id+"F1.opExtrude","SWEPT_BODY",BODY,{"disambiguationData":[OSD([sQuery(id+"F0.wireOp",EDGE,"E0.bottom"),sQuery(id+"F0.wireOp",EDGE,"E0.top"),sQuery(id+"F0.wireOp",EDGE,"E3"),sQuery(id+"F0.wireOp",EDGE,"E4")])]})});
            var Q6;
            Q6=makeQuery(id+"F13.opBoolean","SPLIT",BODY,{"disambiguationData":[OD(7.0)],"derivedFrom":makeQuery(id+"F1.opExtrude","SWEPT_BODY",BODY,{"disambiguationData":[OSD([sQuery(id+"F0.wireOp",EDGE,"E0.bottom"),sQuery(id+"F0.wireOp",EDGE,"E0.top"),sQuery(id+"F0.wireOp",EDGE,"E3"),sQuery(id+"F0.wireOp",EDGE,"E4")])]})});
            var Q7;
            Q7=makeQuery(id+"F13.opBoolean","SPLIT",BODY,{"disambiguationData":[OD(8.0)],"derivedFrom":makeQuery(id+"F1.opExtrude","SWEPT_BODY",BODY,{"disambiguationData":[OSD([sQuery(id+"F0.wireOp",EDGE,"E0.bottom"),sQuery(id+"F0.wireOp",EDGE,"E0.top"),sQuery(id+"F0.wireOp",EDGE,"E3"),sQuery(id+"F0.wireOp",EDGE,"E4")])]})});
            var Q8;
            Q8=makeQuery(id+"F13.opBoolean","SPLIT",BODY,{"disambiguationData":[OD(6.0)],"derivedFrom":makeQuery(id+"F1.opExtrude","SWEPT_BODY",BODY,{"disambiguationData":[OSD([sQuery(id+"F0.wireOp",EDGE,"E0.bottom"),sQuery(id+"F0.wireOp",EDGE,"E0.top"),sQuery(id+"F0.wireOp",EDGE,"E3"),sQuery(id+"F0.wireOp",EDGE,"E4")])]})});
            var Q9;
            Q9=makeQuery(id+"F13.opBoolean","SPLIT",BODY,{"disambiguationData":[OD(2.0)],"derivedFrom":makeQuery(id+"F1.opExtrude","SWEPT_BODY",BODY,{"disambiguationData":[OSD([sQuery(id+"F0.wireOp",EDGE,"E0.bottom"),sQuery(id+"F0.wireOp",EDGE,"E0.top"),sQuery(id+"F0.wireOp",EDGE,"E3"),sQuery(id+"F0.wireOp",EDGE,"E4")])]})});
            var Q10;
            Q10=makeQuery(id+"F13.opBoolean","SPLIT",BODY,{"disambiguationData":[OD(1.0)],"derivedFrom":makeQuery(id+"F1.opExtrude","SWEPT_BODY",BODY,{"disambiguationData":[OSD([sQuery(id+"F0.wireOp",EDGE,"E0.bottom"),sQuery(id+"F0.wireOp",EDGE,"E0.top"),sQuery(id+"F0.wireOp",EDGE,"E3"),sQuery(id+"F0.wireOp",EDGE,"E4")])]})});
            var Q11;
            Q11=makeQuery(id+"F13.opBoolean","SPLIT",BODY,{"disambiguationData":[OD(0.0)],"derivedFrom":makeQuery(id+"F1.opExtrude","SWEPT_BODY",BODY,{"disambiguationData":[OSD([sQuery(id+"F0.wireOp",EDGE,"E0.bottom"),sQuery(id+"F0.wireOp",EDGE,"E0.top"),sQuery(id+"F0.wireOp",EDGE,"E3"),sQuery(id+"F0.wireOp",EDGE,"E4")])]})});
            var Q12;
            Q12=makeQuery(id+"F13.opBoolean","SPLIT",BODY,{"disambiguationData":[OD(9.0)],"derivedFrom":makeQuery(id+"F1.opExtrude","SWEPT_BODY",BODY,{"disambiguationData":[OSD([sQuery(id+"F0.wireOp",EDGE,"E0.bottom"),sQuery(id+"F0.wireOp",EDGE,"E0.top"),sQuery(id+"F0.wireOp",EDGE,"E3"),sQuery(id+"F0.wireOp",EDGE,"E4")])]})});
            var Q13;
            Q13=makeQuery(id+"F13.opBoolean","SPLIT",BODY,{"disambiguationData":[OD(11.0)],"derivedFrom":makeQuery(id+"F1.opExtrude","SWEPT_BODY",BODY,{"disambiguationData":[OSD([sQuery(id+"F0.wireOp",EDGE,"E0.bottom"),sQuery(id+"F0.wireOp",EDGE,"E0.top"),sQuery(id+"F0.wireOp",EDGE,"E3"),sQuery(id+"F0.wireOp",EDGE,"E4")])]})});
            var Q14;
            Q14=makeQuery(id+"F13.opBoolean","SPLIT",BODY,{"disambiguationData":[OD(10.0)],"derivedFrom":makeQuery(id+"F1.opExtrude","SWEPT_BODY",BODY,{"disambiguationData":[OSD([sQuery(id+"F0.wireOp",EDGE,"E0.bottom"),sQuery(id+"F0.wireOp",EDGE,"E0.top"),sQuery(id+"F0.wireOp",EDGE,"E3"),sQuery(id+"F0.wireOp",EDGE,"E4")])]})});
            deleteBodies(context, id + "F14", {"entities" : qUnion([Q0, Q1, Q2, Q3, Q4, Q5, Q6, Q7, Q8, Q9, Q10, Q11, Q12, Q13, Q14])});
        }
    });
